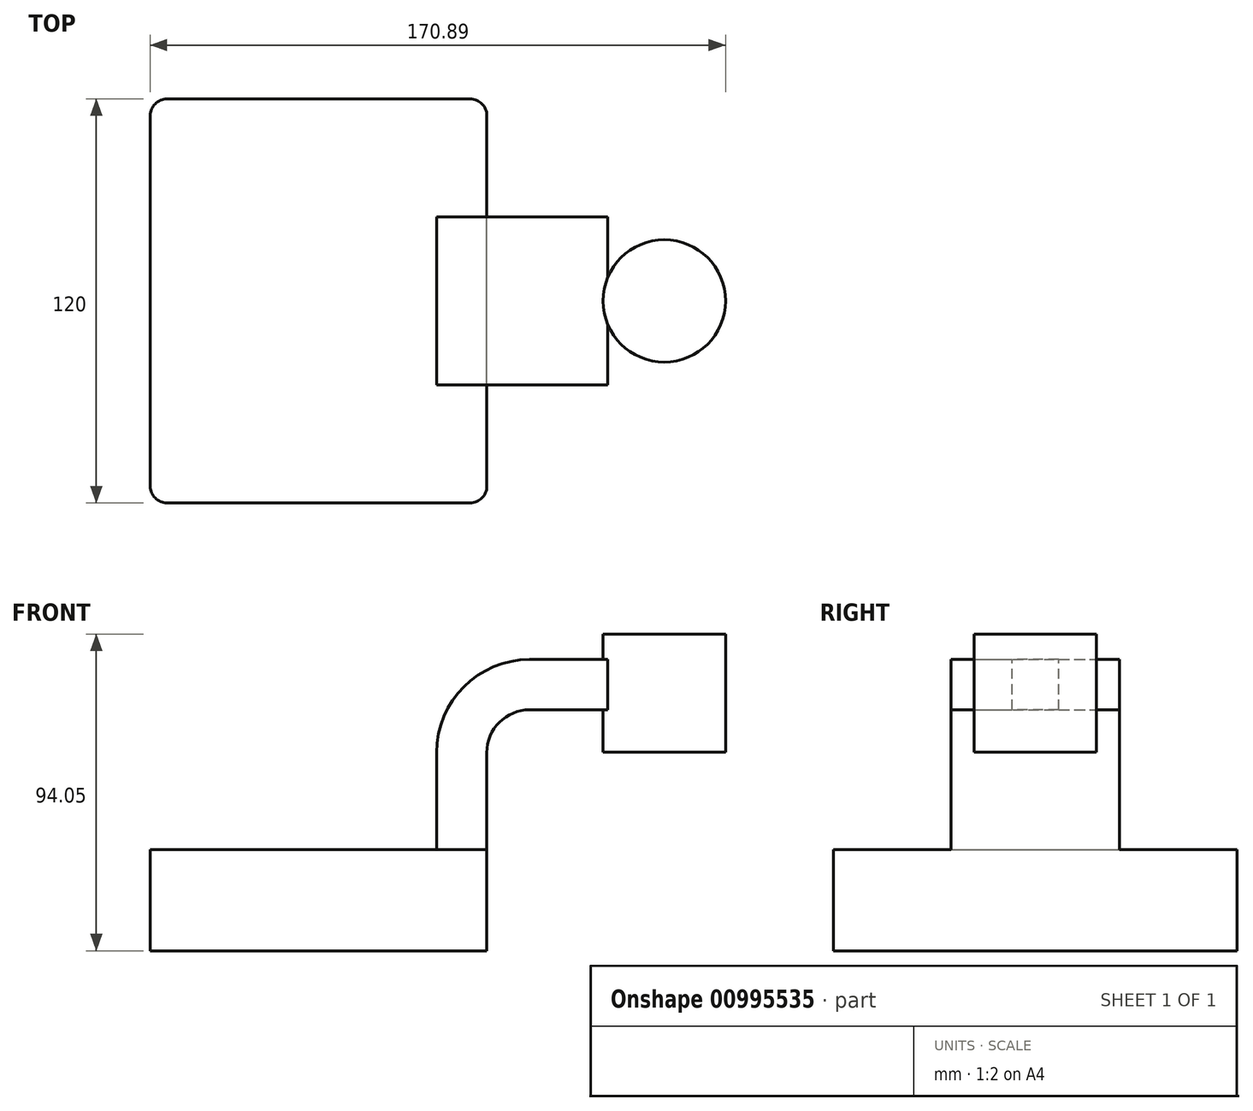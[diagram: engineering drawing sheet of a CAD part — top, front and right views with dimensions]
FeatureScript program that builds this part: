
annotation { "Feature Type Name" : "Feature", "Feature Type Description" : "" }
export const myFeature = defineFeature(function(context is Context, id is Id, definition is map)
    precondition{}
    {
        {
            var Q0;
            Q0=qCreatedBy(makeId("Front.planeOp"),FACE);
            var sketch = newSketch(context, id + "F0", { "sketchPlane" : qUnion([Q0])});
            skLineSegment(sketch, "E0.bottom", {"start": v(-50, 15) * mm, "end": v(50, 15) * mm});
            skLineSegment(sketch, "E0.top", {"start": v(-50, -15) * mm, "end": v(50, -15) * mm});
            skLineSegment(sketch, "E0.left", {"start": v(-50, 15) * mm, "end": v(-50, -15) * mm});
            skLineSegment(sketch, "E0.right", {"start": v(50, 15) * mm, "end": v(50, -15) * mm});
            skPoint(sketch, "E0.middle", {"position": v(0, 0) * mm});
            skLineSegment(sketch, "E1.bottom", {"start": v(120.89, 44.05) * mm, "end": v(85.89, 44.05) * mm});
            skLineSegment(sketch, "E1.top", {"start": v(120.89, 79.05) * mm, "end": v(85.89, 79.05) * mm});
            skLineSegment(sketch, "E1.left", {"start": v(120.89, 44.05) * mm, "end": v(120.89, 79.05) * mm});
            skLineSegment(sketch, "E1.right", {"start": v(85.89, 44.05) * mm, "end": v(85.89, 79.05) * mm});
            skPoint(sketch, "E1.middle", {"position": v(103.39, 61.55) * mm});
            skLineSegment(sketch, "E2", {"start": v(50, 15) * mm, "end": v(50, 43.89) * mm});
            skArc(sketch, "E3", {"start": v(50, 43.89) * mm, "mid": v(53.72, 52.87) * mm, "end": v(62.7, 56.6) * mm});
            skLineSegment(sketch, "E4", {"start": v(62.7, 56.6) * mm, "end": v(102.7, 56.6) * mm});
            skLineSegment(sketch, "E5.0", {"start": v(62.7, 71.52) * mm, "end": v(102.7, 71.52) * mm});
            skArc(sketch, "E5.1", {"start": v(35.08, 43.89) * mm, "mid": v(43.17, 63.42) * mm, "end": v(62.7, 71.52) * mm});
            skLineSegment(sketch, "E5.2", {"start": v(35.08, 15) * mm, "end": v(35.08, 43.89) * mm});
            skLineSegment(sketch, "E6", {"start": v(102.7, 79.05) * mm, "end": v(102.7, 44.05) * mm});
            skPoint(sketch, "E6.endSnap0", {"position": v(103.39, 44.05) * mm});
            skFitSpline(sketch, "E7", {"points": [v(-50, 15) * mm, v(62.7, 71.52) * mm], "startDerivative": vector(75.55, 130.22) * mm, "endDerivative": vector(138.31, -0.78) * mm});
            skSolve(sketch);
        }
        {
            var Q0;
            Q0=makeQuery(id+"F0.imprint","IMPRINT",FACE,{"disambiguationData":[TD([[makeQuery(id+"F0.imprint","IMPRINT",EDGE,{"derivedFrom":sQuery(id+"F0.wireOp",EDGE,"E0.top")}),1.0]])]});
            extrude(context, id + "F1", {"entities" : qUnion([Q0]), "endBound" : BoundingType.SYMMETRIC, "depth" : 120 * mm, "offsetDistance" : 25 * mm});
        }
        {
            var Q0;
            {var subQ1=sQuery(id+"F0.wireOp",EDGE,"E2");Q0=makeQuery(id+"F0.imprint","IMPRINT",FACE,{"disambiguationData":[TD([[makeQuery(id+"F0.imprint","IMPRINT",EDGE,{"derivedFrom":subQ1}),1.0]])]});}
            extrude(context, id + "F2", {"entities" : qUnion([Q0]), "operationType" : NewBodyOperationType.ADD, "endBound" : BoundingType.SYMMETRIC, "depth" : 50 * mm, "offsetDistance" : 25 * mm});
        }
        {
            var Q0;
            Q0=makeQuery(id+"F0.imprint","IMPRINT",FACE,{"disambiguationData":[TD([[makeQuery(id+"F0.imprint","IMPRINT",EDGE,{"derivedFrom":sQuery(id+"F0.wireOp",EDGE,"E5.1")}),1.0]])]});
            extrude(context, id + "F3", {"entities" : qUnion([Q0]), "operationType" : NewBodyOperationType.ADD, "endBound" : BoundingType.SYMMETRIC, "depth" : 5 * mm, "offsetDistance" : 25 * mm});
        }
        {
            var Q0;
            {var subQ4=sQuery(id+"F0.wireOp",EDGE,"E1.left");Q0=makeQuery(id+"F0.imprint","IMPRINT",FACE,{"disambiguationData":[TD([[makeQuery(id+"F0.imprint","IMPRINT",EDGE,{"derivedFrom":subQ4}),1.0]])]});}
            var Q1;
            Q1=sQuery(id+"F0.wireOp",EDGE,"E6");
            revolve(context, id + "F4", {"operationType" : NewBodyOperationType.ADD, "surfaceOperationType" : NewSurfaceOperationType.NEW, "entities" : qUnion([Q0]), "axis" : qUnion([Q1]), "revolveType" : RevolveType.FULL});
        }
        {
            var Q0;
            Q0=makeQuery(id+"F1.opExtrude","CAP_EDGE",EDGE,{"disambiguationData":[OSD([sQuery(id+"F0.wireOp",EDGE,"E0.right")])],"isStart":false});
            var Q1;
            Q1=makeQuery(id+"F1.opExtrude","CAP_EDGE",EDGE,{"disambiguationData":[OSD([sQuery(id+"F0.wireOp",EDGE,"E0.left")])],"isStart":false});
            var Q2;
            Q2=makeQuery(id+"F1.opExtrude","CAP_EDGE",EDGE,{"disambiguationData":[OSD([sQuery(id+"F0.wireOp",EDGE,"E0.right")])],"isStart":true});
            var Q3;
            Q3=makeQuery(id+"F1.opExtrude","CAP_EDGE",EDGE,{"disambiguationData":[OSD([sQuery(id+"F0.wireOp",EDGE,"E0.left")])],"isStart":true});
            fillet(context, id + "F5", {"entities" : qUnion([Q0, Q1, Q2, Q3]), "radius" : 5 * mm, "tangentPropagation" : true, "allowEdgeOverflow" : false});
        }
    });
